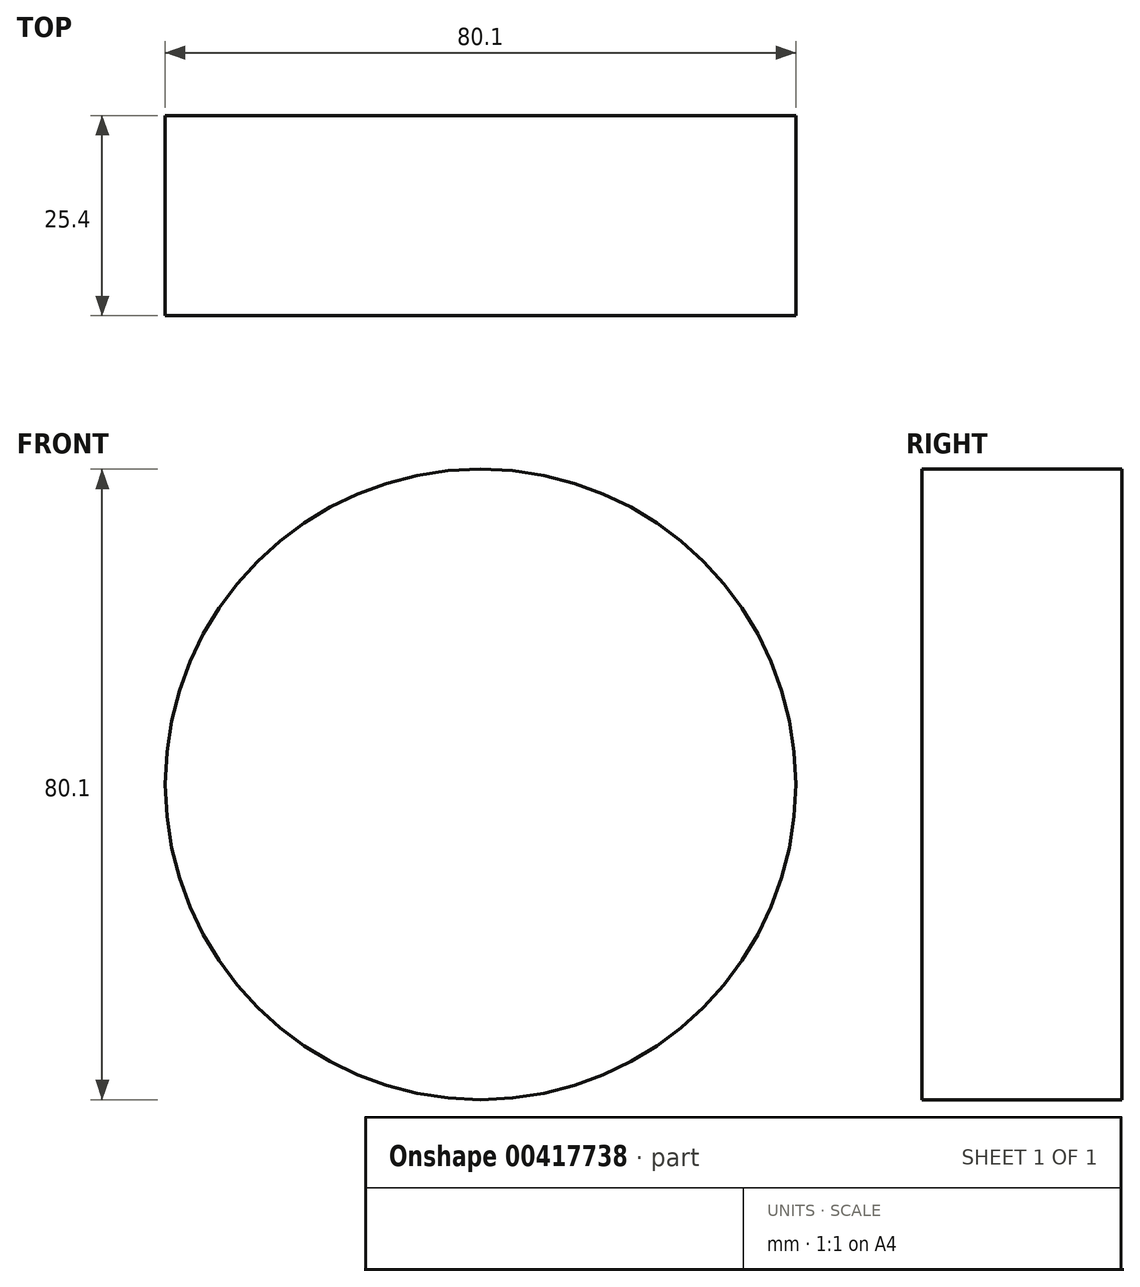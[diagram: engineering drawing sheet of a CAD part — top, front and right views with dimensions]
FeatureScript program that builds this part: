
annotation { "Feature Type Name" : "Feature", "Feature Type Description" : "" }
export const myFeature = defineFeature(function(context is Context, id is Id, definition is map)
    precondition{}
    {
        {
            var Q0;
            Q0=qCreatedBy(makeId("Front.planeOp"),FACE);
            var sketch = newSketch(context, id + "F0", { "sketchPlane" : qUnion([Q0])});
            skCircle(sketch, "E0", {"center": v(0.43, 0.27) * mm, "radius": 40.05 * mm});
            skPoint(sketch, "E0.first.point", {"position": v(0, 40.32) * mm});
            skPoint(sketch, "E0.second.point", {"position": v(31.55, -24.93) * mm});
            skPoint(sketch, "E0.third.point", {"position": v(26.66, 30.53) * mm});
            skSolve(sketch);
        }
        {
            var Q0;
            Q0=makeQuery(id+"F0.imprint","IMPRINT",FACE,{"disambiguationData":[TD([[makeQuery(id+"F0.imprint","IMPRINT",EDGE,{"derivedFrom":sQuery(id+"F0.wireOp",EDGE,"E0")}),1.0]])]});
            extrude(context, id + "F1", {"entities" : qUnion([Q0]), "depth" : 25.4 * mm});
        }
    });
